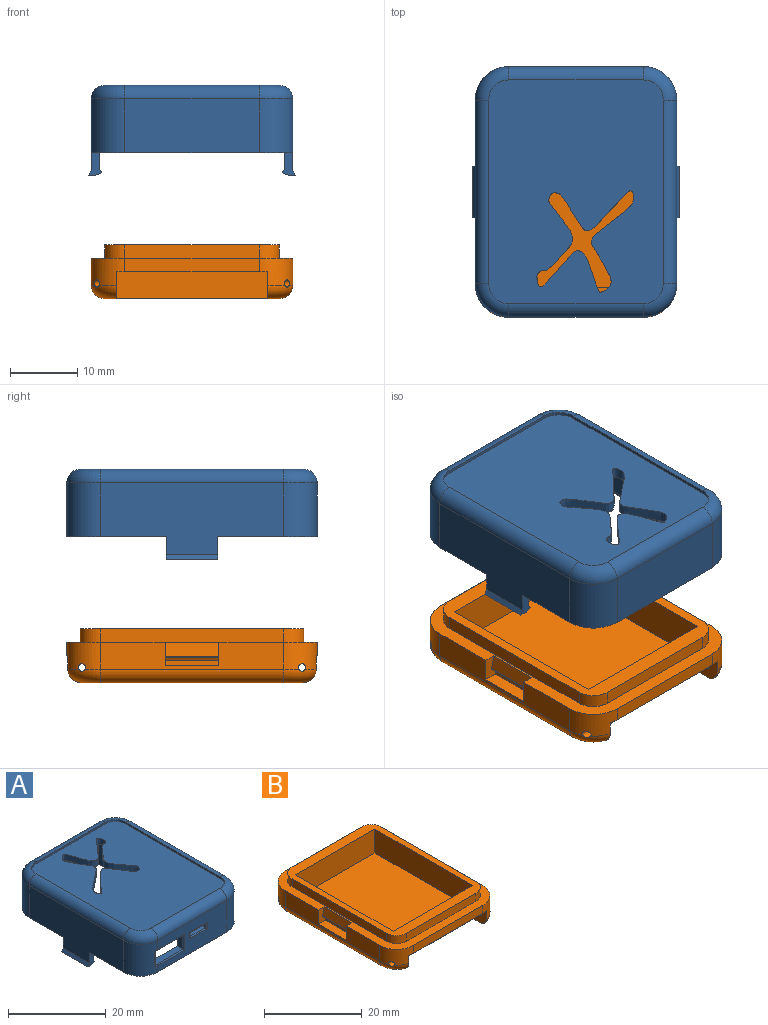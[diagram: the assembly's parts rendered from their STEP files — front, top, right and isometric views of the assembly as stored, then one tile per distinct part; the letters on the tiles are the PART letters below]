
ASSEMBLY  parts=2 mates=2
PART A: 93 faces, bbox 30.8x38.1x13.4 mm
  f0: plane 32.12x23mm, normal (0,0,-1), area 625.6mm2, adj f1,f3,f26,f29,f30,f31,f32,f33
  f1: plane 31.63x6mm, normal (1,0,0), area 185mm2, adj f0,f25,f28,f30,f79,f81
  f2: plane 20x8mm, normal (0,-1,0), area 121mm2, adj f4,f19,f20,f50,f85,f87,f88,f89
  f3: plane 20x8mm, normal (0,1,0), area 128.1mm2, adj f0,f4,f25,f26,f72,f73,f74,f75
  f4: plane 37.3x30mm, normal (0,0,-1), area 198.4mm2, adj f2,f3,f13,f14,f15,f17,f18,f19
  f5: plane 20x0.45mm, normal (0,-1,0), area 9mm2, adj f6,f12,f16,f55
  f6: cylinder r=3mm len=3mm, axis (0,0,1), area 2.1mm2, adj f5,f7,f16,f56
  f7: plane 27.3x0.45mm, normal (-1,0,0), area 12.3mm2, adj f6,f8,f16,f54
  f8: cylinder r=3mm len=3mm, axis (0,0,1), area 2.1mm2, adj f7,f9,f16,f52
  f9: plane 20x0.45mm, normal (0,1,0), area 9mm2, adj f8,f10,f16,f50
  f10: cylinder r=3mm len=3mm, axis (0,0,1), area 2.1mm2, adj f9,f11,f16,f49
  f11: plane 27.3x0.45mm, normal (1,0,0), area 12.3mm2, adj f10,f12,f16,f51
  f12: cylinder r=3mm len=3mm, axis (0,0,1), area 2.1mm2, adj f5,f11,f16,f53
  f13: plane 27.3x10.71mm, normal (1,0,0), area 239mm2, adj f4,f17,f20,f54,f64,f69,f70
  f14: plane 20x8mm, normal (0,1,0), area 160mm2, adj f4,f17,f18,f55
  f15: plane 27.3x10.71mm, normal (-1,0,0), area 239mm2, adj f4,f18,f19,f51,f57,f62,f63
  f16: plane 33.3x26mm, normal (0,0,1), area 806.1mm2, adj f5,f6,f7,f8,f9,f10,f11,f12
  f17: cylinder r=5mm len=8mm, axis (0,0,-1), area 62.8mm2, adj f4,f13,f14,f56
  f18: cylinder r=5mm len=8mm, axis (0,0,1), area 62.8mm2, adj f4,f14,f15,f53
  f19: cylinder r=5mm len=8mm, axis (0,0,-1), area 59.7mm2, adj f2,f4,f15,f49,f83,f84,f86
  f20: cylinder r=5mm len=8mm, axis (0,0,1), area 62.8mm2, adj f2,f4,f13,f52
  f21: cylinder r=3.2mm len=3.2mm, axis (0,0,1), area 10.1mm2, adj f4,f22,f27,f28
  f22: plane 20x2mm, normal (0,-1,0), area 40mm2, adj f4,f21,f23,f28
  f23: cylinder r=3.2mm len=3.2mm, axis (0,0,1), area 10.1mm2, adj f4,f22,f24,f28
  f24: plane 27.3x2mm, normal (1,0,0), area 54.6mm2, adj f4,f23,f25,f28
  f25: cylinder r=3.2mm len=6.7mm, axis (0,0,1), area 15.6mm2, adj f1,f3,f4,f24,f28,f71,f72,f74
  f26: cylinder r=3.2mm len=8mm, axis (0,0,1), area 19.4mm2, adj f0,f3,f4,f27,f28,f29
  f27: plane 27.3x2mm, normal (-1,0,0), area 54.6mm2, adj f4,f21,f26,f28
  f28: plane 33.33x26.4mm, normal (0,0,-1), area 195.2mm2, adj f1,f21,f22,f23,f24,f25,f26,f27
  f29: plane 14.43x6mm, normal (-1,0,0), area 86.6mm2, adj f0,f26,f28,f48
  f30: plane 18x6mm, normal (0,-1,0), area 108mm2, adj f0,f1,f28,f31
  f31: plane 6x2.15mm, normal (-1,0,0), area 12.9mm2, adj f0,f28,f30,f32
  f32: plane 6x5mm, normal (0,-1,0), area 30mm2, adj f0,f28,f31,f33
  f33: plane 6x1.65mm, normal (-1,0,0), area 9.9mm2, adj f0,f28,f32,f34
  f34: plane 6x5.03mm, normal (0,1,0), area 30.2mm2, adj f0,f28,f33,f35
  f35: plane 6x1.35mm, normal (-1,0,0), area 8.1mm2, adj f0,f28,f34,f36
  f36: plane 6x5mm, normal (0,-1,0), area 30mm2, adj f0,f28,f35,f37
  f37: plane 6x1.77mm, normal (-1,0,0), area 10.6mm2, adj f0,f28,f36,f38
  f38: plane 6x4.99mm, normal (0,1,0), area 29.9mm2, adj f0,f28,f37,f39
  f39: plane 6x2.2mm, normal (-1,0,0), area 13.2mm2, adj f0,f28,f38,f40
  f40: plane 6x5mm, normal (0,-1,0), area 30mm2, adj f0,f28,f39,f41
  f41: plane 6x1.83mm, normal (-1,0,0), area 11mm2, adj f0,f28,f40,f42
  f42: plane 6x4.98mm, normal (0,1,0), area 29.9mm2, adj f0,f28,f41,f43
  f43: plane 6x2.2mm, normal (-1,0,0), area 13.2mm2, adj f0,f28,f42,f44
  f44: plane 6x5mm, normal (0,-1,0), area 30mm2, adj f0,f28,f43,f45
  f45: plane 6x2mm, normal (-1,0,0), area 12mm2, adj f0,f28,f44,f46
  f46: plane 6x5mm, normal (0,1,0), area 30mm2, adj f0,f28,f45,f47
  f47: plane 6x2.05mm, normal (-1,0,0), area 12.3mm2, adj f0,f28,f46,f48
  f48: plane 6x5mm, normal (0,-1,0), area 30mm2, adj f0,f28,f29,f47
  f49: torus R=3mm, axis (0,0,1), area 21.1mm2, adj f10,f19,f50,f51
  f50: cylinder r=2mm len=20mm, axis (1,0,0), area 62.8mm2, adj f2,f9,f49,f52
  f51: cylinder r=2mm len=27.3mm, axis (0,-1,0), area 85.8mm2, adj f11,f15,f49,f53
  f52: torus R=3mm, axis (0,0,1), area 21.1mm2, adj f8,f20,f50,f54
  f53: torus R=3mm, axis (0,0,1), area 21.1mm2, adj f12,f18,f51,f55
  f54: cylinder r=2mm len=27.3mm, axis (0,1,0), area 85.8mm2, adj f7,f13,f52,f56
  f55: cylinder r=2mm len=20mm, axis (-1,0,0), area 62.8mm2, adj f5,f14,f53,f56
  f56: torus R=3mm, axis (0,0,1), area 21.1mm2, adj f6,f17,f54,f55
  f57: plane 7.6x0.69mm, normal (-0.87,0,0.5), area 6.1mm2, adj f15,f58,f62,f63
  f58: plane 7.6x1.1mm, normal (0,0,-1), area 8.4mm2, adj f57,f59,f62,f63
  f59: plane 7.6x0.9mm, normal (0.41,0,-0.91), area 7.5mm2, adj f58,f60,f62,f63
  f60: plane 7.6x0.6mm, normal (0.83,0,0.55), area 5.5mm2, adj f59,f61,f62,f63
  f61: plane 7.6x2.4mm, normal (1,0,0), area 18.2mm2, adj f4,f60,f62,f63
  f62: plane 3.4x2mm, normal (0,-1,0), area 4.3mm2, adj f4,f15,f57,f58,f59,f60,f61
  f63: plane 3.4x2mm, normal (0,1,0), area 4.3mm2, adj f4,f15,f57,f58,f59,f60,f61
  f64: plane 7.6x0.69mm, normal (0.87,0,0.5), area 6.1mm2, adj f13,f68,f69,f70
  f65: plane 7.6x2.4mm, normal (-1,0,0), area 18.2mm2, adj f4,f66,f69,f70
  f66: plane 7.6x0.6mm, normal (-0.83,0,0.55), area 5.5mm2, adj f65,f67,f69,f70
  f67: plane 7.6x0.9mm, normal (-0.41,0,-0.91), area 7.5mm2, adj f66,f68,f69,f70
  f68: plane 7.6x1.1mm, normal (0,0,-1), area 8.4mm2, adj f64,f67,f69,f70
  f69: plane 3.4x2mm, normal (0,-1,0), area 4.3mm2, adj f4,f13,f64,f65,f66,f67,f68
  f70: plane 3.4x2mm, normal (0,1,0), area 4.3mm2, adj f4,f13,f64,f65,f66,f67,f68
  f71: plane 3.5x1.53mm, normal (1,0,0), area 5.4mm2, adj f25,f72,f74,f84
  f72: plane 8x1.59mm, normal (0,0,1), area 12.4mm2, adj f3,f25,f71,f73,f83,f84,f85
  f73: plane 3.5x1.55mm, normal (-1,0,0), area 5.4mm2, adj f3,f72,f74,f87
  f74: plane 8x1.59mm, normal (0,0,-1), area 12.4mm2, adj f3,f25,f71,f73,f84,f86,f88
  f75: plane 4.5x1.55mm, normal (0,0,-1), area 7mm2, adj f3,f76,f78,f89
  f76: plane 1.55x1.1mm, normal (1,0,0), area 1.7mm2, adj f3,f75,f77,f90
  f77: plane 4.5x1.55mm, normal (0,0,1), area 7mm2, adj f3,f76,f78,f92
  f78: plane 1.55x1.1mm, normal (-1,0,0), area 1.7mm2, adj f3,f75,f77,f91
  f79: plane 2x1.3mm, normal (0,1,0), area 2.6mm2, adj f0,f1,f80,f81
  f80: plane 4x1.3mm, normal (1,0,0), area 5.2mm2, adj f0,f3,f79,f81
  f81: plane 4x2mm, normal (0,0,-1), area 7.8mm2, adj f1,f3,f25,f79,f80
  f82: extruded ~14.97x14.14mm, area 115mm2, adj f0,f16
  f83: torus R=4.75mm, axis (0,0,-1), area 0.2mm2, adj f19,f72,f84,f85
  f84: cylinder r=0.25mm len=4mm, axis (0,0,-1), area 1.6mm2, adj f19,f71,f72,f74,f83,f86
  f85: cylinder r=0.25mm len=7.75mm, axis (1,0,0), area 3mm2, adj f2,f72,f83,f87
  f86: torus R=4.75mm, axis (0,0,-1), area 0.2mm2, adj f19,f74,f84,f88
  f87: cylinder r=0.25mm len=4mm, axis (0,0,1), area 1.4mm2, adj f2,f73,f85,f88
  f88: cylinder r=0.25mm len=7.75mm, axis (-1,0,0), area 3mm2, adj f2,f74,f86,f87
  f89: cylinder r=0.25mm len=5mm, axis (-1,0,0), area 1.8mm2, adj f2,f75,f90,f91
  f90: cylinder r=0.25mm len=1.6mm, axis (0,0,-1), area 0.5mm2, adj f2,f76,f89,f92
  f91: cylinder r=0.25mm len=1.6mm, axis (0,0,1), area 0.5mm2, adj f2,f78,f89,f92
  f92: cylinder r=0.25mm len=5mm, axis (1,0,0), area 1.8mm2, adj f2,f77,f90,f91
PART B: 58 faces, bbox 30.8x37.8x8 mm
  f0: cylinder r=5mm len=5mm, axis (0,0,1), area 28mm2, adj f3,f4,f6,f7,f30,f33,f54
  f1: cylinder r=5mm len=5mm, axis (0,0,-1), area 28mm2, adj f2,f5,f6,f7,f32,f33,f56
  f2: torus R=3mm, axis (0,0,1), area 16.8mm2, adj f1,f11,f32,f35,f56
  f3: torus R=3mm, axis (0,0,1), area 16.8mm2, adj f0,f11,f30,f37,f54
  f4: plane 27.3x4mm, normal (1,0,0), area 81.2mm2, adj f0,f6,f9,f37,f40,f42,f43
  f5: plane 27.3x4mm, normal (-1,0,0), area 81.2mm2, adj f1,f6,f12,f35,f45,f48,f49
  f6: plane 37.3x30mm, normal (0,0,1), area 213mm2, adj f0,f1,f4,f5,f7,f8,f9,f12
  f7: plane 20x2mm, normal (0,1,0), area 40mm2, adj f0,f1,f6,f33
  f8: plane 20x2mm, normal (0,-1,0), area 40mm2, adj f6,f9,f12,f29
  f9: cylinder r=5mm len=5mm, axis (0,0,-1), area 28mm2, adj f4,f6,f8,f27,f29,f36,f55
  f10: plane 33.3x26mm, normal (0,0,1), area 207.2mm2, adj f13,f14,f15,f16,f17,f18,f19,f20
  f11: plane 32.75x26mm, normal (0,0,-1), area 768.4mm2, adj f2,f3,f26,f27,f28,f30,f31,f32
  f12: cylinder r=5mm len=5mm, axis (0,0,1), area 28mm2, adj f5,f6,f8,f28,f29,f34,f57
  f13: cylinder r=3mm len=3mm, axis (0,0,1), area 9.4mm2, adj f6,f10,f14,f20
  f14: plane 27.3x2mm, normal (1,0,0), area 54.6mm2, adj f6,f10,f13,f15
  f15: cylinder r=3mm len=3mm, axis (0,0,1), area 9.4mm2, adj f6,f10,f14,f16
  f16: plane 20x2mm, normal (0,-1,0), area 40mm2, adj f6,f10,f15,f17
  f17: cylinder r=3mm len=3mm, axis (0,0,1), area 9.4mm2, adj f6,f10,f16,f18
  f18: plane 27.3x2mm, normal (-1,0,0), area 54.6mm2, adj f6,f10,f17,f19
  f19: cylinder r=3mm len=3mm, axis (0,0,1), area 9.4mm2, adj f6,f10,f18,f20
  f20: plane 20x2mm, normal (0,1,0), area 40mm2, adj f6,f10,f13,f19
  f21: plane 28.3x6mm, normal (1,0,0), area 169.8mm2, adj f10,f22,f24,f25
  f22: plane 23x6mm, normal (0,1,0), area 138mm2, adj f10,f21,f23,f25
  f23: plane 28.3x6mm, normal (-1,0,0), area 169.8mm2, adj f10,f22,f24,f25
  f24: plane 23x6mm, normal (0,-1,0), area 138mm2, adj f10,f21,f23,f25
  f25: plane 28.3x23mm, normal (0,0,1), area 650.8mm2, adj f21,f22,f23,f24
  f26: plane 22.5x4mm, normal (0,-1,0), area 90mm2, adj f11,f27,f28,f29
  f27: plane 4x3.84mm, normal (-1,0,0), area 13.5mm2, adj f9,f11,f26,f29,f36,f55
  f28: plane 4x3.84mm, normal (1,0,0), area 13.5mm2, adj f11,f12,f26,f29,f34,f57
  f29: plane 22.5x4mm, normal (0,0,-1), area 89.9mm2, adj f8,f9,f12,f26,f27,f28
  f30: plane 4x3.84mm, normal (-1,0,0), area 13.5mm2, adj f0,f3,f11,f31,f33,f54
  f31: plane 22.5x4mm, normal (0,1,0), area 90mm2, adj f11,f30,f32,f33
  f32: plane 4x3.84mm, normal (1,0,0), area 13.5mm2, adj f1,f2,f11,f31,f33,f56
  f33: plane 22.5x4mm, normal (0,0,-1), area 89.9mm2, adj f0,f1,f7,f30,f31,f32
  f34: torus R=3mm, axis (0,0,1), area 16.8mm2, adj f11,f12,f28,f35,f57
  f35: cylinder r=2mm len=27.3mm, axis (0,-1,0), area 85.8mm2, adj f2,f5,f11,f34
  f36: torus R=3mm, axis (0,0,1), area 16.8mm2, adj f9,f11,f27,f37,f55
  f37: cylinder r=2mm len=27.3mm, axis (0,1,0), area 85.8mm2, adj f3,f4,f11,f36
  f38: plane 8x0.47mm, normal (0.26,0,-0.97), area 3.9mm2, adj f42,f43,f50,f51
  f39: plane 8x0.85mm, normal (1,0,0), area 6.8mm2, adj f40,f42,f43,f50
  f40: plane 8x2mm, normal (0,0,1), area 16mm2, adj f4,f39,f42,f43
  f41: plane 8x2.1mm, normal (0.98,0,0.2), area 17.1mm2, adj f6,f42,f43,f51
  f42: plane 3.5x2mm, normal (0,-1,0), area 5.6mm2, adj f4,f6,f38,f39,f40,f41,f50,f51
  f43: plane 3.5x2mm, normal (0,1,0), area 5.6mm2, adj f4,f6,f38,f39,f40,f41,f50,f51
  f44: plane 8x2.1mm, normal (-0.98,0,0.2), area 17.1mm2, adj f6,f48,f49,f53
  f45: plane 8x2mm, normal (0,0,1), area 16mm2, adj f5,f46,f48,f49
  f46: plane 8x0.85mm, normal (-1,0,0), area 6.8mm2, adj f45,f48,f49,f52
  f47: plane 8x0.47mm, normal (-0.26,0,-0.97), area 3.9mm2, adj f48,f49,f52,f53
  f48: plane 3.5x2mm, normal (0,-1,0), area 5.6mm2, adj f5,f6,f44,f45,f46,f47,f52,f53
  f49: plane 3.5x2mm, normal (0,1,0), area 5.6mm2, adj f5,f6,f44,f45,f46,f47,f52,f53
  f50: cylinder r=0.2mm len=8mm, axis (0,1,0), area 2.1mm2, adj f38,f39,f42,f43
  f51: cylinder r=0.2mm len=8mm, axis (0,-1,0), area 2.4mm2, adj f38,f41,f42,f43
  f52: cylinder r=0.2mm len=8mm, axis (0,1,0), area 2.1mm2, adj f46,f47,f48,f49
  f53: cylinder r=0.2mm len=8mm, axis (0,-1,0), area 2.4mm2, adj f44,f47,f48,f49
  f54: cylinder r=0.55mm len=3.24mm, axis (1,0,0), area 10mm2, adj f0,f3,f30
  f55: cylinder r=0.55mm len=3.24mm, axis (1,0,0), area 10mm2, adj f9,f27,f36
  f56: cylinder r=0.55mm len=3.24mm, axis (1,0,0), area 10mm2, adj f1,f2,f32
  f57: cylinder r=0.55mm len=3.24mm, axis (1,0,0), area 10mm2, adj f12,f28,f34
PLACE A rot(axis=(0,0,1),180deg) t=(-11.27,7.47,32.55)mm
PLACE B t=(-11.27,7.47,0.81)mm fixed
MATE parallel A.f14 <-> B.f8  axis (0,-1,0) through (-11.27,-11.18,26.55)mm
MATE parallel A.f15 <-> B.f4  axis (1,0,0) through (3.73,7.47,26.09)mm
